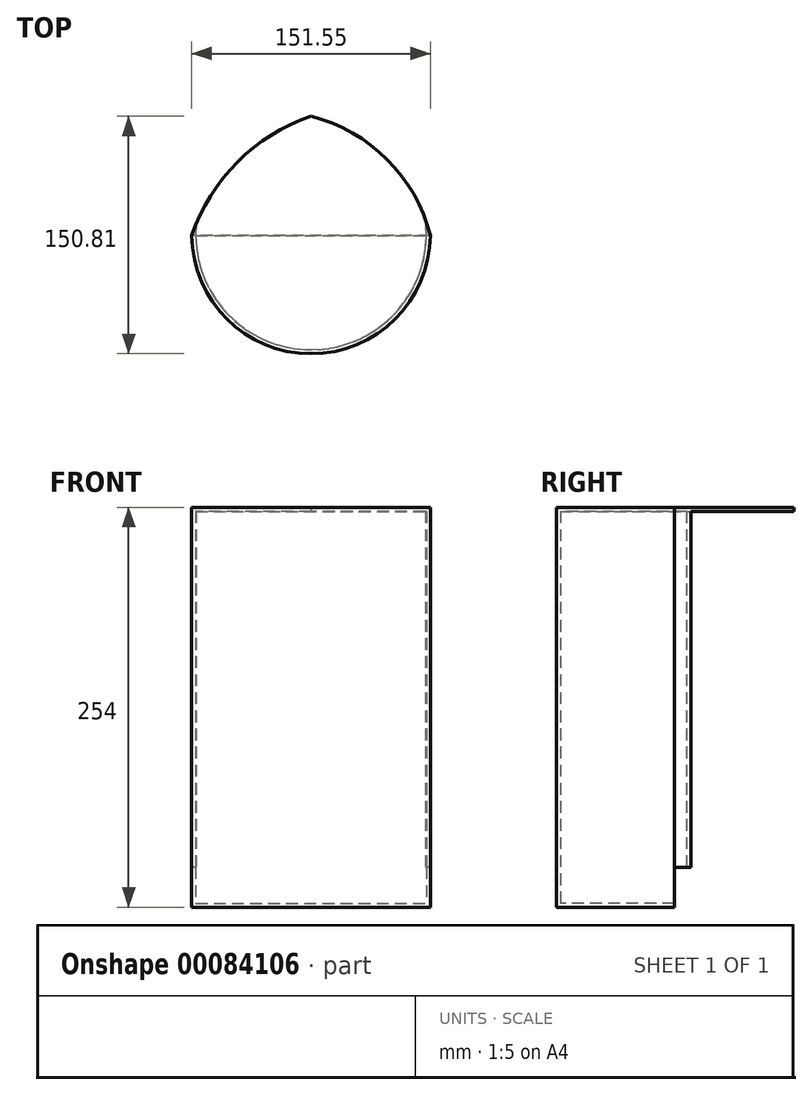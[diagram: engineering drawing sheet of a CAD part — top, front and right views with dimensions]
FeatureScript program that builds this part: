
annotation { "Feature Type Name" : "Feature", "Feature Type Description" : "" }
export const myFeature = defineFeature(function(context is Context, id is Id, definition is map)
    precondition{}
    {
        {
            var Q0;
            Q0=qCreatedBy(makeId("Top.planeOp"),FACE);
            var sketch = newSketch(context, id + "F0", { "sketchPlane" : qUnion([Q0])});
            skPoint(sketch, "E0.end.orphan", {"position": v(-75.96, 0) * mm});
            skPoint(sketch, "E0.start.orphan", {"position": v(75.59, 0) * mm});
            skArc(sketch, "E1", {"start": v(-75.96, 0) * mm, "mid": v(-0.19, -75.04) * mm, "end": v(75.59, 0) * mm});
            skArc(sketch, "E2", {"start": v(-0.19, 75.77) * mm, "mid": v(-46.96, 46.77) * mm, "end": v(-75.96, 0) * mm});
            skPoint(sketch, "E2.startSnap0", {"position": v(-0.19, -75.04) * mm});
            skArc(sketch, "E3", {"start": v(75.59, 0) * mm, "mid": v(48.22, 48.4) * mm, "end": v(-0.19, 75.77) * mm});
            skSolve(sketch);
        }
        {
            var Q0;
            Q0 = qSketchRegion(id + "F0", true);
            extrude(context, id + "F1", {"entities" : qUnion([Q0]), "depth" : 254 * mm});
        }
        {
            var Q0;
            Q0=makeQuery(id+"F1.opExtrude","SWEPT_FACE",FACE,{"disambiguationData":[OSD([sQuery(id+"F0.wireOp",EDGE,"E2")])]});
            var Q1;
            Q1=makeQuery(id+"F1.opExtrude","SWEPT_FACE",FACE,{"disambiguationData":[OSD([sQuery(id+"F0.wireOp",EDGE,"E3")])]});
            shell(context, id + "F2", {"entities" : qUnion([Q0, Q1]), "thickness" : 2.54 * mm});
        }
        {
            var Q0;
            Q0=makeQuery(id+"F1.opExtrude","CAP_FACE",FACE,{"disambiguationData":[OSD([sQuery(id+"F0.wireOp",EDGE,"E1"),sQuery(id+"F0.wireOp",EDGE,"E2"),sQuery(id+"F0.wireOp",EDGE,"E3")])],"isStart":true});
            var sketch = newSketch(context, id + "F3", { "sketchPlane" : qUnion([Q0])});
            skLineSegment(sketch, "E4", {"start": v(75.59, 0) * mm, "end": v(-75.96, 0) * mm});
            skLineSegment(sketch, "E5", {"start": v(-0.19, -75.77) * mm, "end": v(0, 0) * mm});
            skSolve(sketch);
        }
        {
            var Q0;
            {var subQ2=sQuery(id+"F3.wireOp",EDGE,"E5");Q0=makeQuery(id+"F3.imprint","IMPRINT",FACE,{"disambiguationData":[TD([[makeQuery(id+"F3.imprint","IMPRINT",EDGE,{"derivedFrom":subQ2}),-1.0]])]});}
            var Q1;
            {var subQ2=sQuery(id+"F3.wireOp",EDGE,"E5");Q1=makeQuery(id+"F3.imprint","IMPRINT",FACE,{"disambiguationData":[TD([[makeQuery(id+"F3.imprint","IMPRINT",EDGE,{"derivedFrom":subQ2}),1.0]])]});}
            extrude(context, id + "F4", {"entities" : qUnion([Q0, Q1]), "operationType" : NewBodyOperationType.REMOVE, "oppositeDirection" : true, "depth" : 25.4 * mm});
        }
    });
